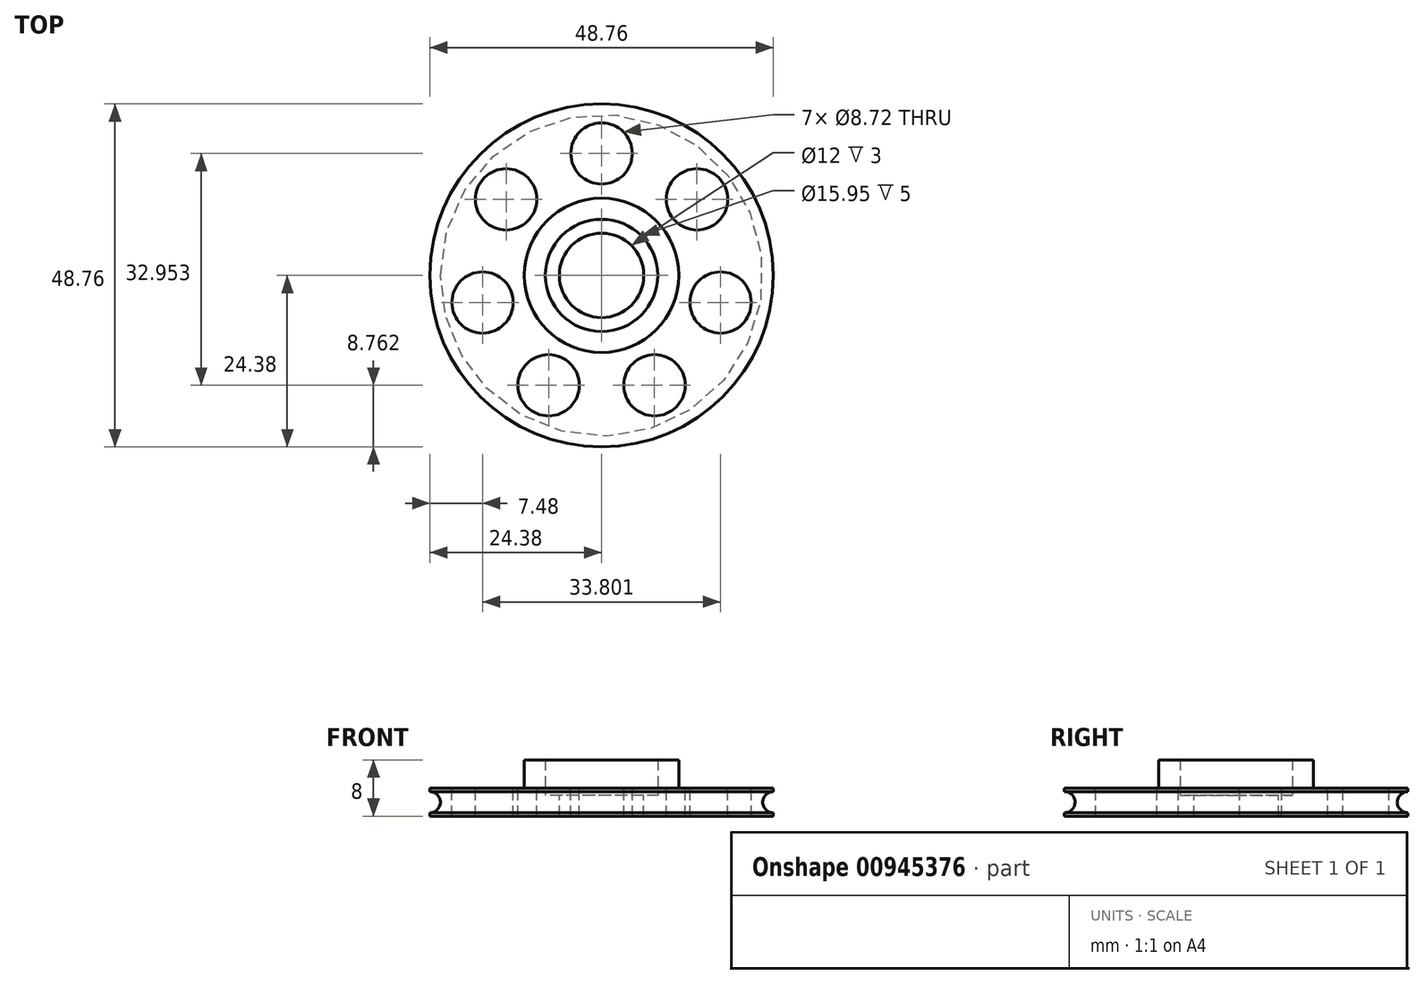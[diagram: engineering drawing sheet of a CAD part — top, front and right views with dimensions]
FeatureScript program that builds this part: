
annotation { "Feature Type Name" : "Feature", "Feature Type Description" : "" }
export const myFeature = defineFeature(function(context is Context, id is Id, definition is map)
    precondition{}
    {
        {
            var Q0;
            Q0=qCreatedBy(makeId("Top.planeOp"),FACE);
            var sketch = newSketch(context, id + "F0", { "sketchPlane" : qUnion([Q0])});
            skCircle(sketch, "E0", {"center": v(0, 0) * mm, "radius": 24.38 * mm});
            skSolve(sketch);
        }
        {
            var Q0;
            Q0=makeQuery(id+"F0.imprint","IMPRINT",FACE,{"disambiguationData":[TD([[makeQuery(id+"F0.imprint","IMPRINT",EDGE,{"derivedFrom":sQuery(id+"F0.wireOp",EDGE,"E0")}),1.0]])]});
            extrude(context, id + "F1", {"entities" : qUnion([Q0]), "depth" : 4 * mm, "offsetDistance" : 25.4 * mm});
        }
        {
            var Q0;
            Q0=makeQuery(id+"F1.opExtrude","CAP_FACE",FACE,{"disambiguationData":[OSD([sQuery(id+"F0.wireOp",EDGE,"E0"),sQuery(id+"F0.wireOp",EDGE,"n39IqKt5-bk1q-LU1x-fgod-8OyBNiFTd7FZ")])],"isStart":false});
            var sketch = newSketch(context, id + "F2", { "sketchPlane" : qUnion([Q0])});
            skCircle(sketch, "E1", {"center": v(0, 0) * mm, "radius": 7.97 * mm});
            skCircle(sketch, "E2.0", {"center": v(0, 0) * mm, "radius": 10.97 * mm});
            skSolve(sketch);
        }
        {
            var Q0;
            Q0=qSketchRegion(id+"F2",true);
            extrude(context, id + "F3", {"entities" : qUnion([Q0]), "operationType" : NewBodyOperationType.ADD, "depth" : 4 * mm, "offsetDistance" : 25.4 * mm});
        }
        {
            var Q0;
            Q0=makeQuery(id+"F3.boolean.opBoolean","SPLIT",FACE,{"disambiguationData":[TD([makeQuery(id+"F3.opExtrude","SWEPT_FACE",FACE,{"disambiguationData":[OSD([sQuery(id+"F2.wireOp",EDGE,"E1")])]})])],"derivedFrom":makeQuery(id+"F1.opExtrude","CAP_FACE",FACE,{"disambiguationData":[OSD([sQuery(id+"F0.wireOp",EDGE,"E0")])],"isStart":false})});
            var sketch = newSketch(context, id + "F4", { "sketchPlane" : qUnion([Q0])});
            skCircle(sketch, "E3", {"center": v(0, 0) * mm, "radius": 6 * mm});
            skSolve(sketch);
        }
        {
            var Q0;
            Q0=makeQuery(id+"F4.imprint","IMPRINT",FACE,{"disambiguationData":[TD([[makeQuery(id+"F4.imprint","IMPRINT",EDGE,{"derivedFrom":sQuery(id+"F4.wireOp",EDGE,"E3")}),1.0]])]});
            var Q1;
            Q1=makeQuery(id+"F4.imprint","IMPRINT",FACE,{"disambiguationData":[TD([[makeQuery(id+"F4.imprint","IMPRINT",EDGE,{"derivedFrom":makeQuery(id+"FgYK8jIepfClWtA_1.opExtrude","CAP_EDGE",EDGE,{"disambiguationData":[OSD([sQuery(id+"F8DXjnVyigKkjng_1.wireOp",EDGE,"EUjAMsCd-Zx2B-3j4q-cP5o-T3GrjTijNDqK")])],"isStart":false})}),1.0]])]});
            extrude(context, id + "F5", {"entities" : qUnion([Q0, Q1]), "operationType" : NewBodyOperationType.REMOVE, "oppositeDirection" : true, "depth" : 9 * mm, "offsetDistance" : 25.4 * mm});
        }
        {
            var Q0;
            Q0=qCreatedBy(makeId("Front.planeOp"),FACE);
            var sketch = newSketch(context, id + "F6", { "sketchPlane" : qUnion([Q0])});
            skCircle(sketch, "E4", {"center": v(-24.38, 2) * mm, "radius": 1.5 * mm});
            skLineSegment(sketch, "E5.bottom", {"start": v(-22.88, 0.65) * mm, "end": v(-25.02, 0.65) * mm});
            skLineSegment(sketch, "E5.top", {"start": v(-22.88, 3.35) * mm, "end": v(-25.02, 3.35) * mm});
            skLineSegment(sketch, "E5.left", {"start": v(-22.88, 0.65) * mm, "end": v(-22.88, 3.35) * mm});
            skLineSegment(sketch, "E5.right", {"start": v(-25.73, 1.35) * mm, "end": v(-25.73, 2.65) * mm});
            skLineSegment(sketch, "E6", {"start": v(0, 19.1) * mm, "end": v(0, -12.61) * mm, "construction": true});
            skLineSegment(sketch, "E7", {"start": v(-24.37, 3.35) * mm, "end": v(-22.88, 2) * mm});
            skLineSegment(sketch, "E8", {"start": v(-22.88, 2) * mm, "end": v(-24.38, 0.65) * mm});
            skLineSegment(sketch, "E9", {"start": v(-24.38, 0.65) * mm, "end": v(-24.37, 3.35) * mm});
            skSolve(sketch);
        }
        {
            var Q0;
            {var subQ0=sQuery(id+"F6.wireOp",EDGE,"E5.top");var subQ1=sQuery(id+"F6.wireOp",EDGE,"E4");var subQ2=makeQuery(id+"F6.imprint","INTERSECT",VERTEX,{"disambiguationData":[OD(0.0)],"derivedFrom":[subQ1,subQ0]});Q0=makeQuery(id+"F6.imprint","IMPRINT",FACE,{"disambiguationData":[TD([[makeQuery(id+"F6.imprint","IMPRINT",EDGE,{"disambiguationData":[TD([[subQ2,1.0]])],"derivedFrom":subQ1}),1.0]])]});}
            var Q1;
            {var subQ0=sQuery(id+"F6.wireOp",EDGE,"E5.bottom");var subQ1=sQuery(id+"F6.wireOp",EDGE,"E4");var subQ2=makeQuery(id+"F6.imprint","INTERSECT",VERTEX,{"disambiguationData":[OD(0.0)],"derivedFrom":[subQ1,subQ0]});Q1=makeQuery(id+"F6.imprint","IMPRINT",FACE,{"disambiguationData":[TD([[makeQuery(id+"F6.imprint","IMPRINT",EDGE,{"disambiguationData":[TD([[subQ2,-1.0]])],"derivedFrom":subQ1}),1.0]])]});}
            var Q2;
            {var subQ4=sQuery(id+"F6.wireOp",EDGE,"E5.right");Q2=makeQuery(id+"F6.imprint","IMPRINT",FACE,{"disambiguationData":[TD([[makeQuery(id+"F6.imprint","IMPRINT",EDGE,{"derivedFrom":subQ4}),-1.0]])]});}
            var Q3;
            {var subQ0=sQuery(id+"F6.wireOp",EDGE,"E7");Q3=makeQuery(id+"F6.imprint","IMPRINT",FACE,{"disambiguationData":[TD([[makeQuery(id+"F6.imprint","IMPRINT",EDGE,{"derivedFrom":subQ0}),1.0]])]});}
            var Q4;
            Q4=makeQuery(id+"F6.imprint","IMPRINT",FACE,{"disambiguationData":[TD([[makeQuery(id+"F6.imprint","IMPRINT",EDGE,{"derivedFrom":sQuery(id+"F6.wireOp",EDGE,"E7")}),-1.0]])]});
            var Q5;
            {var subQ0=sQuery(id+"F6.wireOp",EDGE,"E8");Q5=makeQuery(id+"F6.imprint","IMPRINT",FACE,{"disambiguationData":[TD([[makeQuery(id+"F6.imprint","IMPRINT",EDGE,{"derivedFrom":subQ0}),1.0]])]});}
            var Q6;
            Q6=sQuery(id+"F6.wireOp",EDGE,"E6");
            revolve(context, id + "F7", {"operationType" : NewBodyOperationType.REMOVE, "surfaceOperationType" : NewSurfaceOperationType.NEW, "entities" : qUnion([Q0, Q1, Q2, Q3, Q4, Q5]), "axis" : qUnion([Q6]), "revolveType" : RevolveType.FULL, "oppositeDirection" : true});
        }
        {
            var Q0;
            Q0=makeQuery(id+"F3.boolean.opBoolean","SPLIT",FACE,{"disambiguationData":[TD([makeQuery(id+"F3.opExtrude","SWEPT_FACE",FACE,{"disambiguationData":[OSD([sQuery(id+"F2.wireOp",EDGE,"E1")])]})])],"derivedFrom":makeQuery(id+"F1.opExtrude","CAP_FACE",FACE,{"disambiguationData":[OSD([sQuery(id+"F0.wireOp",EDGE,"E0")])],"isStart":false})});
            extrude(context, id + "F8", {"entities" : qUnion([Q0]), "operationType" : NewBodyOperationType.REMOVE, "oppositeDirection" : true, "depth" : 1 * mm, "offsetDistance" : 25 * mm});
        }
        {
            var Q0;
            {var subQ0=sQuery(id+"F0.wireOp",EDGE,"E0");Q0=makeQuery(id+"F3.boolean.opBoolean","SPLIT",FACE,{"disambiguationData":[TD([makeQuery(id+"F1.opExtrude","SWEPT_FACE",FACE,{"disambiguationData":[OSD([subQ0])]})])],"derivedFrom":makeQuery(id+"F1.opExtrude","CAP_FACE",FACE,{"disambiguationData":[OSD([subQ0])],"isStart":false})});}
            var sketch = newSketch(context, id + "F9", { "sketchPlane" : qUnion([Q0])});
            skCircle(sketch, "E10", {"center": v(0, 17.34) * mm, "radius": 4.36 * mm});
            skCircle(sketch, "E11.1.0", {"center": v(-13.55, 10.8) * mm, "radius": 4.36 * mm});
            skCircle(sketch, "E11.2.0", {"center": v(-16.9, -3.86) * mm, "radius": 4.36 * mm});
            skCircle(sketch, "E11.3.0", {"center": v(-7.52, -15.62) * mm, "radius": 4.36 * mm});
            skCircle(sketch, "E11.4.0", {"center": v(7.52, -15.62) * mm, "radius": 4.36 * mm});
            skCircle(sketch, "E11.5.0", {"center": v(16.9, -3.86) * mm, "radius": 4.36 * mm});
            skCircle(sketch, "E11.6.0", {"center": v(13.55, 10.8) * mm, "radius": 4.36 * mm});
            skPoint(sketch, "E11.center", {"position": v(0, 0) * mm});
            skSolve(sketch);
        }
        {
            var Q0;
            Q0 = qSketchRegion(id + "F9", true);
            extrude(context, id + "F10", {"entities" : qUnion([Q0]), "operationType" : NewBodyOperationType.REMOVE, "oppositeDirection" : true, "depth" : 25 * mm, "offsetDistance" : 25 * mm});
        }
    });
